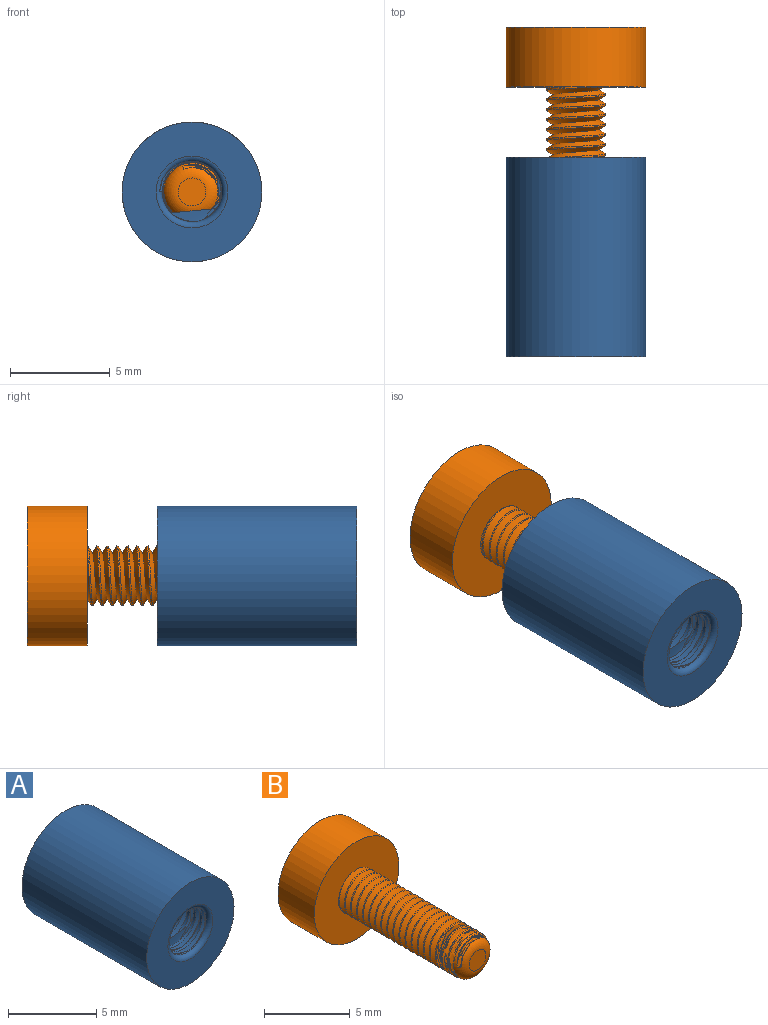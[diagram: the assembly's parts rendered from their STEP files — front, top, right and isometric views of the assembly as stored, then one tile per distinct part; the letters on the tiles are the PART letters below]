
ASSEMBLY  parts=2 mates=1
PART A: 9 faces, bbox 7x10.2x7 mm
  f0: cylinder r=1.5mm len=9.4mm, axis (0,1,0), area 45.5mm2, adj f1,f5,f6,f7,f8
  f1: torus R=1.8mm, axis (0,-1,0), area 4mm2, adj f0,f3,f6,f7
  f2: cylinder r=3.5mm len=10mm, axis (0,1,0), area 219.9mm2, adj f3,f4
  f3: plane 7x7mm, normal (0,-1,0), area 28.3mm2, adj f1,f2
  f4: plane 7x7mm, normal (0,1,0), area 28.3mm2, adj f2,f5
  f5: torus R=1.8mm, axis (0,-1,0), area 3.1mm2, adj f0,f4,f7,f8
  f6: plane 0.27x0.24mm, normal (0,0,1), area 0mm2, adj f0,f1,f7,f8
  f7: bspline ~10.07x4.08mm, area 61.4mm2, adj f0,f1,f5,f6,f8
  f8: bspline ~10.07x4.08mm, area 60.6mm2, adj f0,f5,f6,f7
PART B: 12 faces, bbox 7x13x7 mm
  f0: cylinder r=1.5mm len=9.2mm, axis (0,1,0), area 15.2mm2, adj f2,f5,f6,f10,f11
  f1: cylinder r=3.5mm len=7mm, axis (0,1,0), area 66mm2, adj f2,f3
  f2: plane 7x7mm, normal (0,-1,0), area 31.4mm2, adj f0,f1,f9
  f3: plane 7x7mm, normal (0,1,0), area 38.5mm2, adj f1
  f4: plane 1.4x1.4mm, normal (0,-1,0), area 1.5mm2, adj f5
  f5: torus R=0.7mm, axis (0,-1,0), area 5.8mm2, adj f0,f4,f6,f7,f10,f11
  f6: torus R=0.7mm, axis (0,-1,0), area 0mm2, adj f0,f5,f11
  f7: plane 0.21x0.16mm, normal (0,0,1), area 0mm2, adj f5,f10,f11
  f8: plane 0.42x0.36mm, normal (0,0,-1), area 0.1mm2, adj f9,f10,f11
  f9: cylinder r=1.5mm len=3mm, axis (0,1,0), area 1.7mm2, adj f2,f8,f11
  f10: bspline ~10.21x3.46mm, area 67.5mm2, adj f0,f5,f7,f8,f11
  f11: bspline ~10.21x3.46mm, area 69.3mm2, adj f0,f5,f6,f7,f8,f9,f10
PLACE A t=(-3.83,2.35,-0.5)mm fixed
PLACE B rot(axis=(0,1,0),70deg) t=(-3.83,8.86,-0.5)mm
MATE cylindrical B.f0 <-> A.f0  axis (0,-1,0) through (-3.83,5.86,-0.5)mm
